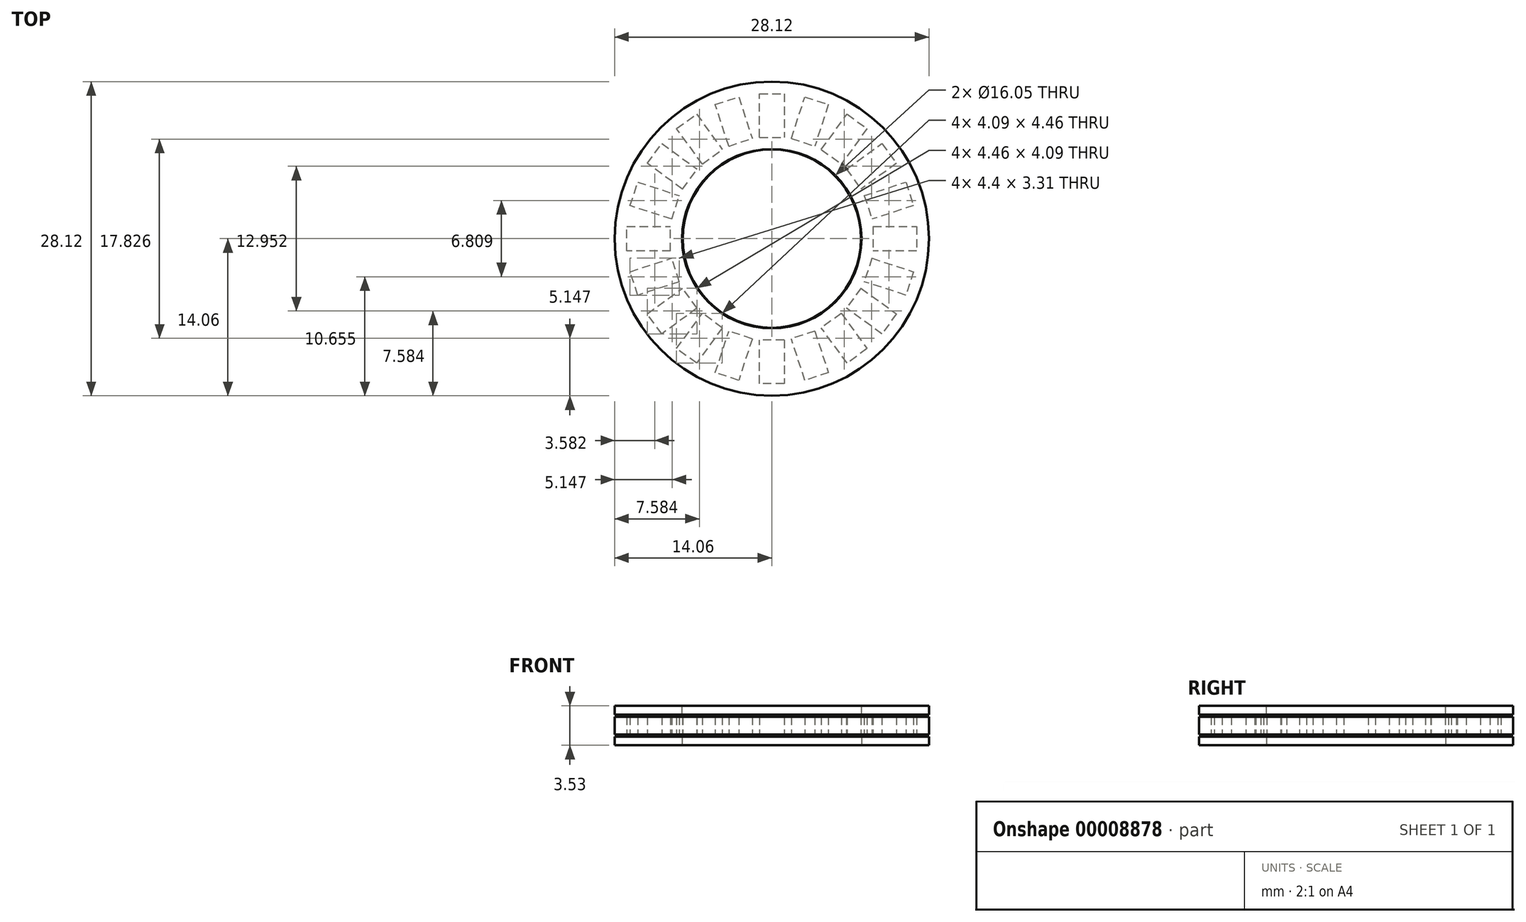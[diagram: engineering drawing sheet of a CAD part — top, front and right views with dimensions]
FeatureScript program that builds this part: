
annotation { "Feature Type Name" : "Feature", "Feature Type Description" : "" }
export const myFeature = defineFeature(function(context is Context, id is Id, definition is map)
    precondition{}
    {
        {
            var Q0;
            Q0=qCreatedBy(makeId("Top.planeOp"),FACE);
            var sketch = newSketch(context, id + "F0", { "sketchPlane" : qUnion([Q0])});
            skCircle(sketch, "E0", {"center": v(0, 0) * mm, "radius": 8.03 * mm});
            skCircle(sketch, "E1", {"center": v(0, 0) * mm, "radius": 14.06 * mm});
            skSolve(sketch);
        }
        {
            var Q0;
            Q0=makeQuery(id+"F0.imprint","IMPRINT",FACE,{"disambiguationData":[TD([[makeQuery(id+"F0.imprint","IMPRINT",EDGE,{"derivedFrom":sQuery(id+"F0.wireOp",EDGE,"E0")}),-1.0]])]});
            extrude(context, id + "F1", {"entities" : qUnion([Q0]), "depth" : 0.79 * mm});
        }
        {
            var Q0;
            Q0=makeQuery(id+"F1.opExtrude","CAP_FACE",FACE,{"disambiguationData":[OSD([sQuery(id+"F0.wireOp",EDGE,"E0"),sQuery(id+"F0.wireOp",EDGE,"E1")])],"isStart":false});
            cPlane(context, id + "F2", {"entities" : qUnion([Q0]), "cplaneType" : CPlaneType.OFFSET, "offset" : 0.98 * mm, "width" : 152.4 * mm, "height" : 152.4 * mm});
        }
        {
            var Q0;
            Q0=qCreatedBy(id+"F2.planeOp",FACE);
            var sketch = newSketch(context, id + "F3", { "sketchPlane" : qUnion([Q0])});
            skCircle(sketch, "E2", {"center": v(0, 0) * mm, "radius": 7.98 * mm});
            skCircle(sketch, "E3", {"center": v(0, 0) * mm, "radius": 14.06 * mm});
            skLineSegment(sketch, "E4", {"start": v(0, 14.06) * mm, "end": v(0, 7.98) * mm, "construction": true});
            skLineSegment(sketch, "E5", {"start": v(-0.98, 11.02) * mm, "end": v(0.98, 11.02) * mm, "construction": true});
            skPoint(sketch, "E6", {"position": v(0, 11.02) * mm});
            skLineSegment(sketch, "E7.0", {"start": v(-0.98, 9.19) * mm, "end": v(0, 9.19) * mm, "construction": true});
            skLineSegment(sketch, "E8.0.MirrorCS", {"start": v(-0.98, 12.85) * mm, "end": v(0, 12.85) * mm, "construction": true});
            skLineSegment(sketch, "E9", {"start": v(0.98, 12.85) * mm, "end": v(0.98, 9.19) * mm, "construction": true});
            skLineSegment(sketch, "E10", {"start": v(-0.98, 9.19) * mm, "end": v(-0.98, 12.85) * mm, "construction": true});
            skLineSegment(sketch, "E11.0", {"start": v(-1.1, 12.97) * mm, "end": v(1.1, 12.97) * mm});
            skLineSegment(sketch, "E11.1", {"start": v(-1.1, 9.06) * mm, "end": v(-1.1, 12.97) * mm});
            skLineSegment(sketch, "E11.2", {"start": v(-1.1, 9.06) * mm, "end": v(1.1, 9.06) * mm});
            skLineSegment(sketch, "E11.3", {"start": v(1.1, 12.97) * mm, "end": v(1.1, 9.06) * mm});
            skLineSegment(sketch, "E12.1.0", {"start": v(-3.85, 8.28) * mm, "end": v(-5.06, 12) * mm});
            skLineSegment(sketch, "E12.1.1", {"start": v(-5.06, 12) * mm, "end": v(-2.96, 12.68) * mm});
            skLineSegment(sketch, "E12.1.2", {"start": v(-2.96, 12.68) * mm, "end": v(-1.75, 8.96) * mm});
            skLineSegment(sketch, "E12.1.3", {"start": v(-3.85, 8.28) * mm, "end": v(-1.75, 8.96) * mm});
            skLineSegment(sketch, "E12.2.0", {"start": v(-6.22, 6.68) * mm, "end": v(-8.52, 9.85) * mm});
            skLineSegment(sketch, "E12.2.1", {"start": v(-8.52, 9.85) * mm, "end": v(-6.73, 11.14) * mm});
            skLineSegment(sketch, "E12.2.2", {"start": v(-6.73, 11.14) * mm, "end": v(-4.43, 7.98) * mm});
            skLineSegment(sketch, "E12.2.3", {"start": v(-6.22, 6.68) * mm, "end": v(-4.43, 7.98) * mm});
            skLineSegment(sketch, "E12.3.0", {"start": v(-7.98, 4.43) * mm, "end": v(-11.14, 6.73) * mm});
            skLineSegment(sketch, "E12.3.1", {"start": v(-11.14, 6.73) * mm, "end": v(-9.85, 8.52) * mm});
            skLineSegment(sketch, "E12.3.2", {"start": v(-9.85, 8.52) * mm, "end": v(-6.68, 6.22) * mm});
            skLineSegment(sketch, "E12.3.3", {"start": v(-7.98, 4.43) * mm, "end": v(-6.68, 6.22) * mm});
            skLineSegment(sketch, "E12.4.0", {"start": v(-8.96, 1.75) * mm, "end": v(-12.68, 2.96) * mm});
            skLineSegment(sketch, "E12.4.1", {"start": v(-12.68, 2.96) * mm, "end": v(-12, 5.06) * mm});
            skLineSegment(sketch, "E12.4.2", {"start": v(-12, 5.06) * mm, "end": v(-8.28, 3.85) * mm});
            skLineSegment(sketch, "E12.4.3", {"start": v(-8.96, 1.75) * mm, "end": v(-8.28, 3.85) * mm});
            skLineSegment(sketch, "E12.5.0", {"start": v(-9.06, -1.1) * mm, "end": v(-12.97, -1.1) * mm});
            skLineSegment(sketch, "E12.5.1", {"start": v(-12.97, -1.1) * mm, "end": v(-12.97, 1.1) * mm});
            skLineSegment(sketch, "E12.5.2", {"start": v(-12.97, 1.1) * mm, "end": v(-9.06, 1.1) * mm});
            skLineSegment(sketch, "E12.5.3", {"start": v(-9.06, -1.1) * mm, "end": v(-9.06, 1.1) * mm});
            skLineSegment(sketch, "E12.6.0", {"start": v(-8.28, -3.85) * mm, "end": v(-12, -5.06) * mm});
            skLineSegment(sketch, "E12.6.1", {"start": v(-12, -5.06) * mm, "end": v(-12.68, -2.96) * mm});
            skLineSegment(sketch, "E12.6.2", {"start": v(-12.68, -2.96) * mm, "end": v(-8.96, -1.75) * mm});
            skLineSegment(sketch, "E12.6.3", {"start": v(-8.28, -3.85) * mm, "end": v(-8.96, -1.75) * mm});
            skLineSegment(sketch, "E12.7.0", {"start": v(-6.68, -6.22) * mm, "end": v(-9.85, -8.52) * mm});
            skLineSegment(sketch, "E12.7.1", {"start": v(-9.85, -8.52) * mm, "end": v(-11.14, -6.73) * mm});
            skLineSegment(sketch, "E12.7.2", {"start": v(-11.14, -6.73) * mm, "end": v(-7.98, -4.43) * mm});
            skLineSegment(sketch, "E12.7.3", {"start": v(-6.68, -6.22) * mm, "end": v(-7.98, -4.43) * mm});
            skLineSegment(sketch, "E12.8.0", {"start": v(-4.43, -7.98) * mm, "end": v(-6.73, -11.14) * mm});
            skLineSegment(sketch, "E12.8.1", {"start": v(-6.73, -11.14) * mm, "end": v(-8.52, -9.85) * mm});
            skLineSegment(sketch, "E12.8.2", {"start": v(-8.52, -9.85) * mm, "end": v(-6.22, -6.68) * mm});
            skLineSegment(sketch, "E12.8.3", {"start": v(-4.43, -7.98) * mm, "end": v(-6.22, -6.68) * mm});
            skLineSegment(sketch, "E12.9.0", {"start": v(-1.75, -8.96) * mm, "end": v(-2.96, -12.68) * mm});
            skLineSegment(sketch, "E12.9.1", {"start": v(-2.96, -12.68) * mm, "end": v(-5.06, -12) * mm});
            skLineSegment(sketch, "E12.9.2", {"start": v(-5.06, -12) * mm, "end": v(-3.85, -8.28) * mm});
            skLineSegment(sketch, "E12.9.3", {"start": v(-1.75, -8.96) * mm, "end": v(-3.85, -8.28) * mm});
            skLineSegment(sketch, "E12.10.0", {"start": v(1.1, -9.06) * mm, "end": v(1.1, -12.97) * mm});
            skLineSegment(sketch, "E12.10.1", {"start": v(1.1, -12.97) * mm, "end": v(-1.1, -12.97) * mm});
            skLineSegment(sketch, "E12.10.2", {"start": v(-1.1, -12.97) * mm, "end": v(-1.1, -9.06) * mm});
            skLineSegment(sketch, "E12.10.3", {"start": v(1.1, -9.06) * mm, "end": v(-1.1, -9.06) * mm});
            skLineSegment(sketch, "E12.11.0", {"start": v(3.85, -8.28) * mm, "end": v(5.06, -12) * mm});
            skLineSegment(sketch, "E12.11.1", {"start": v(5.06, -12) * mm, "end": v(2.96, -12.68) * mm});
            skLineSegment(sketch, "E12.11.2", {"start": v(2.96, -12.68) * mm, "end": v(1.75, -8.96) * mm});
            skLineSegment(sketch, "E12.11.3", {"start": v(3.85, -8.28) * mm, "end": v(1.75, -8.96) * mm});
            skLineSegment(sketch, "E12.12.0", {"start": v(6.22, -6.68) * mm, "end": v(8.52, -9.85) * mm});
            skLineSegment(sketch, "E12.12.1", {"start": v(8.52, -9.85) * mm, "end": v(6.73, -11.14) * mm});
            skLineSegment(sketch, "E12.12.2", {"start": v(6.73, -11.14) * mm, "end": v(4.43, -7.98) * mm});
            skLineSegment(sketch, "E12.12.3", {"start": v(6.22, -6.68) * mm, "end": v(4.43, -7.98) * mm});
            skLineSegment(sketch, "E12.13.0", {"start": v(7.98, -4.43) * mm, "end": v(11.14, -6.73) * mm});
            skLineSegment(sketch, "E12.13.1", {"start": v(11.14, -6.73) * mm, "end": v(9.85, -8.52) * mm});
            skLineSegment(sketch, "E12.13.2", {"start": v(9.85, -8.52) * mm, "end": v(6.68, -6.22) * mm});
            skLineSegment(sketch, "E12.13.3", {"start": v(7.98, -4.43) * mm, "end": v(6.68, -6.22) * mm});
            skLineSegment(sketch, "E12.14.0", {"start": v(8.96, -1.75) * mm, "end": v(12.68, -2.96) * mm});
            skLineSegment(sketch, "E12.14.1", {"start": v(12.68, -2.96) * mm, "end": v(12, -5.06) * mm});
            skLineSegment(sketch, "E12.14.2", {"start": v(12, -5.06) * mm, "end": v(8.28, -3.85) * mm});
            skLineSegment(sketch, "E12.14.3", {"start": v(8.96, -1.75) * mm, "end": v(8.28, -3.85) * mm});
            skLineSegment(sketch, "E12.15.0", {"start": v(9.06, 1.1) * mm, "end": v(12.97, 1.1) * mm});
            skLineSegment(sketch, "E12.15.1", {"start": v(12.97, 1.1) * mm, "end": v(12.97, -1.1) * mm});
            skLineSegment(sketch, "E12.15.2", {"start": v(12.97, -1.1) * mm, "end": v(9.06, -1.1) * mm});
            skLineSegment(sketch, "E12.15.3", {"start": v(9.06, 1.1) * mm, "end": v(9.06, -1.1) * mm});
            skLineSegment(sketch, "E12.16.0", {"start": v(8.28, 3.85) * mm, "end": v(12, 5.06) * mm});
            skLineSegment(sketch, "E12.16.1", {"start": v(12, 5.06) * mm, "end": v(12.68, 2.96) * mm});
            skLineSegment(sketch, "E12.16.2", {"start": v(12.68, 2.96) * mm, "end": v(8.96, 1.75) * mm});
            skLineSegment(sketch, "E12.16.3", {"start": v(8.28, 3.85) * mm, "end": v(8.96, 1.75) * mm});
            skLineSegment(sketch, "E12.17.0", {"start": v(6.68, 6.22) * mm, "end": v(9.85, 8.52) * mm});
            skLineSegment(sketch, "E12.17.1", {"start": v(9.85, 8.52) * mm, "end": v(11.14, 6.73) * mm});
            skLineSegment(sketch, "E12.17.2", {"start": v(11.14, 6.73) * mm, "end": v(7.98, 4.43) * mm});
            skLineSegment(sketch, "E12.17.3", {"start": v(6.68, 6.22) * mm, "end": v(7.98, 4.43) * mm});
            skLineSegment(sketch, "E12.18.0", {"start": v(4.43, 7.98) * mm, "end": v(6.73, 11.14) * mm});
            skLineSegment(sketch, "E12.18.1", {"start": v(6.73, 11.14) * mm, "end": v(8.52, 9.85) * mm});
            skLineSegment(sketch, "E12.18.2", {"start": v(8.52, 9.85) * mm, "end": v(6.22, 6.68) * mm});
            skLineSegment(sketch, "E12.18.3", {"start": v(4.43, 7.98) * mm, "end": v(6.22, 6.68) * mm});
            skLineSegment(sketch, "E12.19.0", {"start": v(1.75, 8.96) * mm, "end": v(2.96, 12.68) * mm});
            skLineSegment(sketch, "E12.19.1", {"start": v(2.96, 12.68) * mm, "end": v(5.06, 12) * mm});
            skLineSegment(sketch, "E12.19.2", {"start": v(5.06, 12) * mm, "end": v(3.85, 8.28) * mm});
            skLineSegment(sketch, "E12.19.3", {"start": v(1.75, 8.96) * mm, "end": v(3.85, 8.28) * mm});
            skLineSegment(sketch, "E13", {"start": v(0, 12.85) * mm, "end": v(0.98, 12.85) * mm, "construction": true});
            skLineSegment(sketch, "E14", {"start": v(0, 9.19) * mm, "end": v(0.98, 9.19) * mm, "construction": true});
            skSolve(sketch);
        }
        {
            var Q0;
            Q0=makeQuery(id+"F3.imprint","IMPRINT",FACE,{"disambiguationData":[TD([[makeQuery(id+"F3.imprint","IMPRINT",EDGE,{"derivedFrom":sQuery(id+"F3.wireOp",EDGE,"E3")}),1.0]])]});
            extrude(context, id + "F4", {"entities" : qUnion([Q0]), "endBound" : BoundingType.SYMMETRIC, "depth" : 1.6 * mm});
        }
        {
            var Q0;
            Q0=makeQuery(id+"F1.opExtrude","SWEPT_BODY",BODY,{"disambiguationData":[OSD([sQuery(id+"F0.wireOp",EDGE,"E0"),sQuery(id+"F0.wireOp",EDGE,"E1")])]});
            var Q1;
            Q1=qCreatedBy(id+"F2.planeOp",FACE);
            mirror(context, id + "F5", {"entities" : qUnion([Q0]), "mirrorPlane" : qUnion([Q1])});
        }
    });
